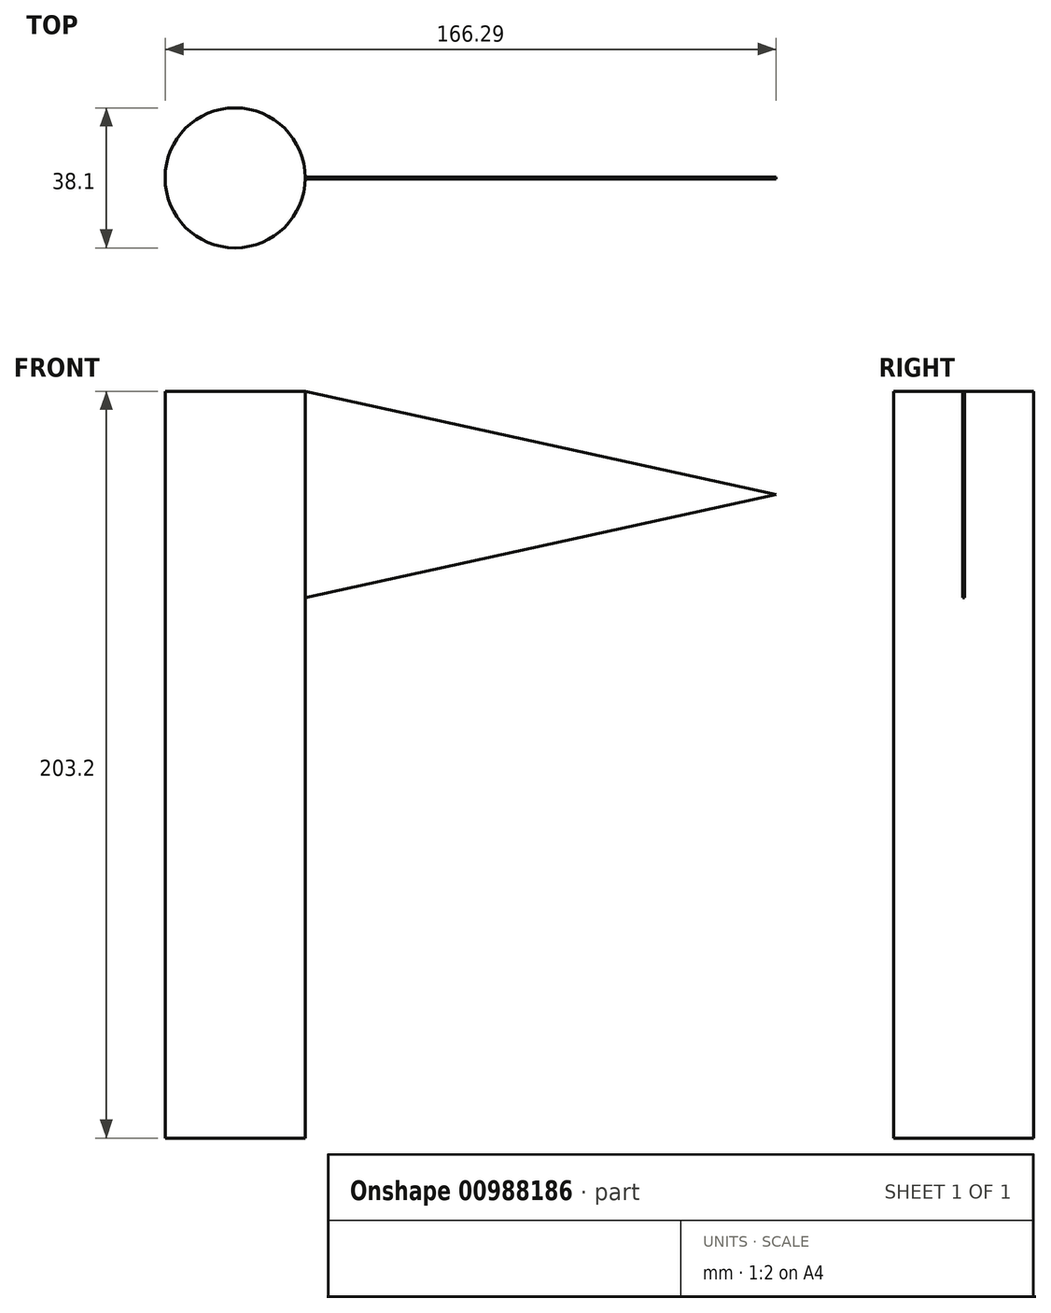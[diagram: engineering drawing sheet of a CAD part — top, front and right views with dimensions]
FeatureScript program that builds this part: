
annotation { "Feature Type Name" : "Feature", "Feature Type Description" : "" }
export const myFeature = defineFeature(function(context is Context, id is Id, definition is map)
    precondition{}
    {
        {
            var Q0;
            Q0=qCreatedBy(makeId("Top.planeOp"),FACE);
            var sketch = newSketch(context, id + "F0", { "sketchPlane" : qUnion([Q0])});
            skCircle(sketch, "E0", {"center": v(0, 0) * mm, "radius": 19.05 * mm});
            skSolve(sketch);
        }
        {
            var Q0;
            Q0=qSketchRegion(id+"F0",true);
            extrude(context, id + "F1", {"entities" : qUnion([Q0]), "depth" : 203.2 * mm, "offsetDistance" : 25.4 * mm});
        }
        {
            var Q0;
            Q0=qCreatedBy(makeId("Front.planeOp"),FACE);
            var sketch = newSketch(context, id + "F2", { "sketchPlane" : qUnion([Q0])});
            skLineSegment(sketch, "E1.0", {"start": v(-19.05, 203.2) * mm, "end": v(19.05, 203.2) * mm, "construction": true});
            skLineSegment(sketch, "E2", {"start": v(19.05, 203.2) * mm, "end": v(19.05, 0) * mm, "construction": true});
            skLineSegment(sketch, "E3", {"start": v(19.05, 203.2) * mm, "end": v(147.24, 175.12) * mm});
            skLineSegment(sketch, "E4", {"start": v(147.24, 175.12) * mm, "end": v(73.2, 175.12) * mm, "construction": true});
            skLineSegment(sketch, "E5.MirrorCS", {"start": v(19.05, 147.04) * mm, "end": v(147.24, 175.12) * mm});
            skLineSegment(sketch, "E6", {"start": v(19.05, 147.04) * mm, "end": v(19.05, 203.2) * mm});
            skLineSegment(sketch, "E7", {"start": v(19.05, 203.2) * mm, "end": v(11.75, 180.87) * mm});
            skLineSegment(sketch, "E8", {"start": v(11.75, 180.87) * mm, "end": v(19.05, 147.04) * mm});
            skSolve(sketch);
        }
        {
            var Q0;
            Q0=makeQuery(id+"F2.imprint","IMPRINT",FACE,{"disambiguationData":[TD([[makeQuery(id+"F2.imprint","IMPRINT",EDGE,{"derivedFrom":sQuery(id+"F2.wireOp",EDGE,"E3")}),-1.0]])]});
            var Q1;
            Q1=makeQuery(id+"F2.imprint","IMPRINT",FACE,{"disambiguationData":[TD([[makeQuery(id+"F2.imprint","IMPRINT",EDGE,{"derivedFrom":sQuery(id+"F2.wireOp",EDGE,"E6")}),1.0]])]});
            extrude(context, id + "F3", {"entities" : qUnion([Q0, Q1]), "operationType" : NewBodyOperationType.ADD, "depth" : 0.5 * mm, "offsetDistance" : 25.4 * mm, "symmetric" : true});
        }
    });
